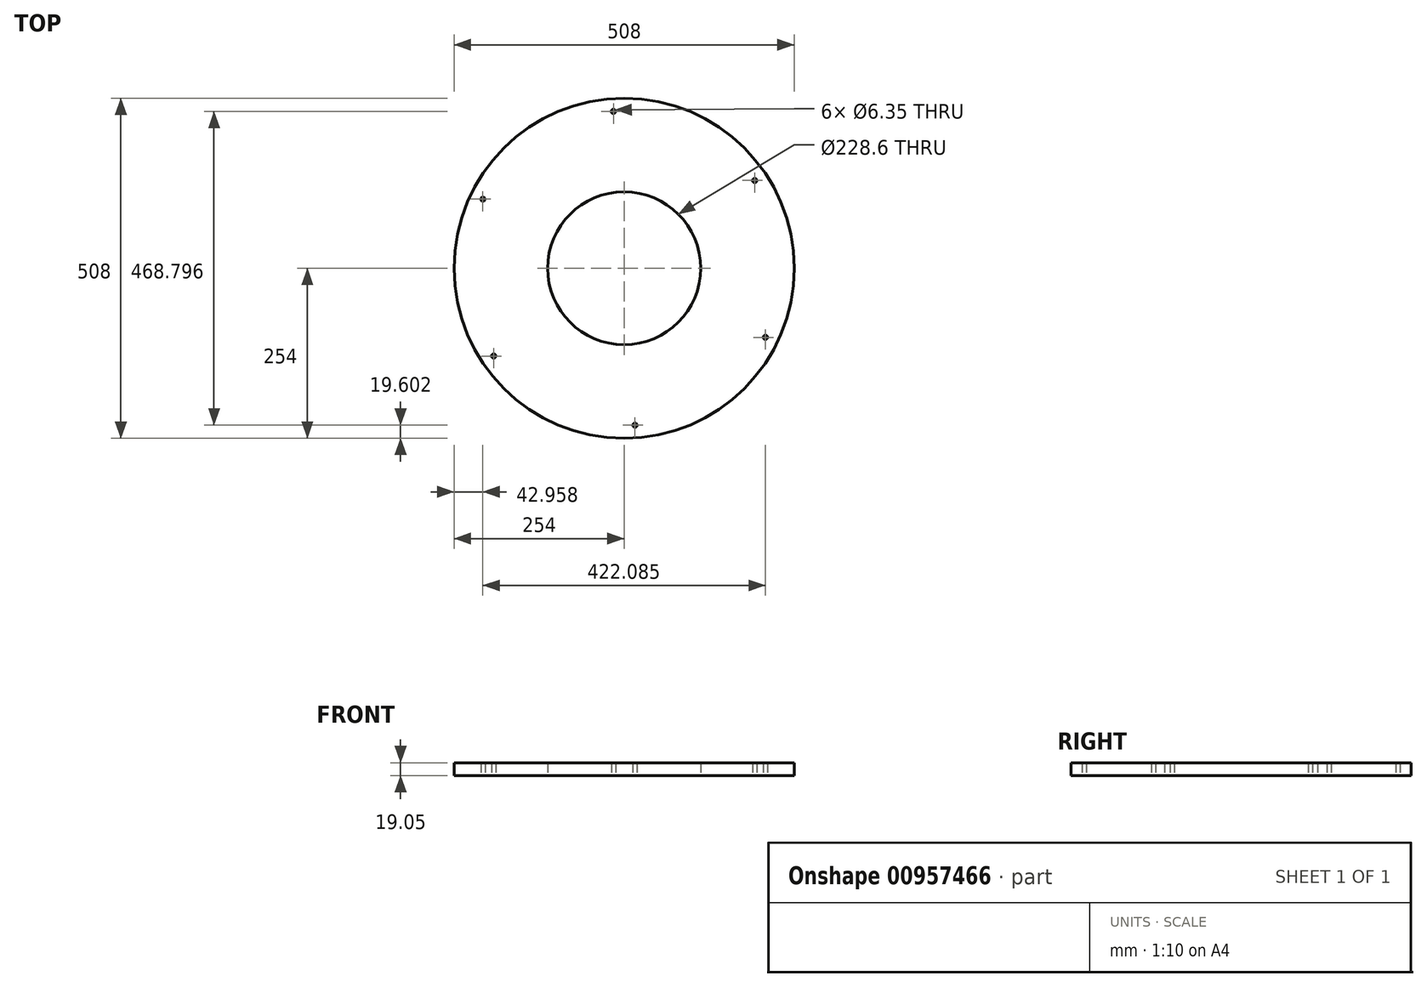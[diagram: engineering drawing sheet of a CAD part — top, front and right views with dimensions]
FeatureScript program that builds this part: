
annotation { "Feature Type Name" : "Feature", "Feature Type Description" : "" }
export const myFeature = defineFeature(function(context is Context, id is Id, definition is map)
    precondition{}
    {
        {
            var Q0;
            Q0=qCreatedBy(makeId("Top.planeOp"),FACE);
            var sketch = newSketch(context, id + "F0", { "sketchPlane" : qUnion([Q0])});
            skCircle(sketch, "E0", {"center": v(0, 0) * mm, "radius": 254 * mm});
            skCircle(sketch, "E1", {"center": v(0, 0) * mm, "radius": 234.95 * mm});
            skCircle(sketch, "E2", {"center": v(-211.04, 103.26) * mm, "radius": 3.18 * mm});
            skCircle(sketch, "E3.1.0", {"center": v(-194.95, -131.14) * mm, "radius": 3.18 * mm});
            skCircle(sketch, "E3.2.0", {"center": v(16.1, -234.4) * mm, "radius": 3.18 * mm});
            skCircle(sketch, "E4.1.3.0", {"center": v(211.04, -103.26) * mm, "radius": 3.18 * mm});
            skCircle(sketch, "E4.1.4.0", {"center": v(194.95, 131.14) * mm, "radius": 3.18 * mm});
            skCircle(sketch, "E4.1.5.0", {"center": v(-16.1, 234.4) * mm, "radius": 3.18 * mm});
            skCircle(sketch, "E5", {"center": v(0, 0) * mm, "radius": 114.3 * mm});
            skSolve(sketch);
        }
        {
            var Q0;
            {var subQ0=sQuery(id+"F0.wireOp",EDGE,"E1");var subQ1=sQuery(id+"F0.wireOp",EDGE,"E2");var subQ5=makeQuery(id+"F0.imprint","INTERSECT",VERTEX,{"disambiguationData":[OD(0.0)],"derivedFrom":[subQ1,subQ0]});Q0=makeQuery(id+"F0.imprint","IMPRINT",FACE,{"disambiguationData":[TD([[makeQuery(id+"F0.imprint","IMPRINT",EDGE,{"disambiguationData":[TD([[subQ5,1.0]])],"derivedFrom":subQ1}),-1.0]])]});}
            var Q1;
            Q1=makeQuery(id+"F0.imprint","IMPRINT",FACE,{"disambiguationData":[TD([[makeQuery(id+"F0.imprint","IMPRINT",EDGE,{"derivedFrom":sQuery(id+"F0.wireOp",EDGE,"E0")}),1.0]])]});
            extrude(context, id + "F1", {"entities" : qUnion([Q0, Q1]), "depth" : 19.05 * mm, "offsetDistance" : 25.4 * mm});
        }
    });
